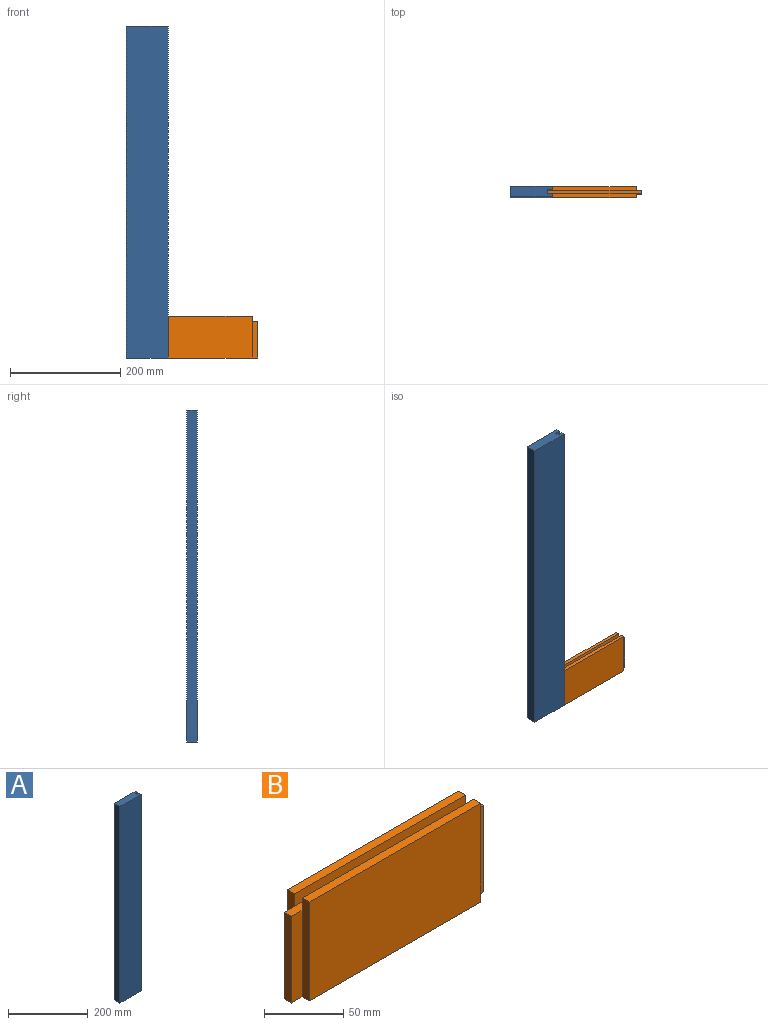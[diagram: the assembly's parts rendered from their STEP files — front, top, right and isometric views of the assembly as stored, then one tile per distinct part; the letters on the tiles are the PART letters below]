
ASSEMBLY  parts=2 mates=1
PART A: 10 faces, bbox 76.2x19.1x603.3 mm
  f0: plane 603.25x6.35mm, normal (1,0,0), area 3830.6mm2, adj f1,f2,f5,f7
  f1: plane 76.2x19.05mm, normal (0,0,-1), area 1391.1mm2, adj f0,f3,f4,f5,f6,f7,f8,f9
  f2: plane 76.2x19.05mm, normal (0,0,1), area 1391.1mm2, adj f0,f3,f4,f5,f6,f7,f8,f9
  f3: plane 603.25x19.05mm, normal (-1,0,0), area 11491.9mm2, adj f1,f2,f5,f6
  f4: plane 603.25x6.35mm, normal (1,0,0), area 3830.6mm2, adj f1,f2,f6,f9
  f5: plane 603.25x76.2mm, normal (0,-1,0), area 45967.6mm2, adj f0,f1,f2,f3
  f6: plane 603.25x76.2mm, normal (0,1,0), area 45967.6mm2, adj f1,f2,f3,f4
  f7: plane 603.25x9.53mm, normal (0,1,0), area 5746mm2, adj f0,f1,f2,f8
  f8: plane 603.25x6.35mm, normal (1,0,0), area 3830.6mm2, adj f1,f2,f7,f9
  f9: plane 603.25x9.53mm, normal (0,-1,0), area 5746mm2, adj f1,f2,f4,f8
PART B: 18 faces, bbox 171.5x19.1x76.2 mm
  f0: plane 76.2x6.35mm, normal (1,0,0), area 483.9mm2, adj f2,f5,f7,f11,f15
  f1: plane 76.2x6.35mm, normal (-1,0,0), area 483.9mm2, adj f2,f5,f7,f11,f13
  f2: plane 152.4x6.35mm, normal (0,0,1), area 967.7mm2, adj f0,f1,f7,f11
  f3: plane 76.2x6.35mm, normal (1,0,0), area 483.9mm2, adj f5,f6,f8,f9,f16
  f4: plane 76.2x6.35mm, normal (-1,0,0), area 483.9mm2, adj f5,f6,f8,f9,f12
  f5: plane 171.45x19.05mm, normal (0,0,-1), area 3024.2mm2, adj f0,f1,f3,f4,f7,f8,f12,f13
  f6: plane 152.4x6.35mm, normal (0,0,1), area 967.7mm2, adj f3,f4,f8,f9
  f7: plane 152.4x76.2mm, normal (0,-1,0), area 11612.9mm2, adj f0,f1,f2,f5
  f8: plane 152.4x76.2mm, normal (0,1,0), area 11612.9mm2, adj f3,f4,f5,f6
  f9: plane 152.4x9.53mm, normal (0,-1,0), area 1451.6mm2, adj f3,f4,f6,f10
  f10: plane 171.45x6.35mm, normal (0,0,1), area 1088.7mm2, adj f9,f11,f12,f13,f14,f15,f16,f17
  f11: plane 152.4x9.53mm, normal (0,1,0), area 1451.6mm2, adj f0,f1,f2,f10
  f12: plane 66.68x9.53mm, normal (0,1,0), area 635.1mm2, adj f4,f5,f10,f14
  f13: plane 66.68x9.53mm, normal (0,-1,0), area 635.1mm2, adj f1,f5,f10,f14
  f14: plane 66.68x6.35mm, normal (-1,0,0), area 423.4mm2, adj f5,f10,f12,f13
  f15: plane 66.68x9.53mm, normal (0,-1,0), area 635.1mm2, adj f0,f5,f10,f17
  f16: plane 66.68x9.53mm, normal (0,1,0), area 635.1mm2, adj f3,f5,f10,f17
  f17: plane 66.68x6.35mm, normal (1,0,0), area 423.4mm2, adj f5,f10,f15,f16
PLACE A t=(-286.28,1.82,-98.25)mm fixed
PLACE B t=(-210.08,1.82,-98.25)mm
MATE fastened A.f8 <-> B.f14  axis (-1,0,0) through (-219.6,-10.88,-98.25)mm
